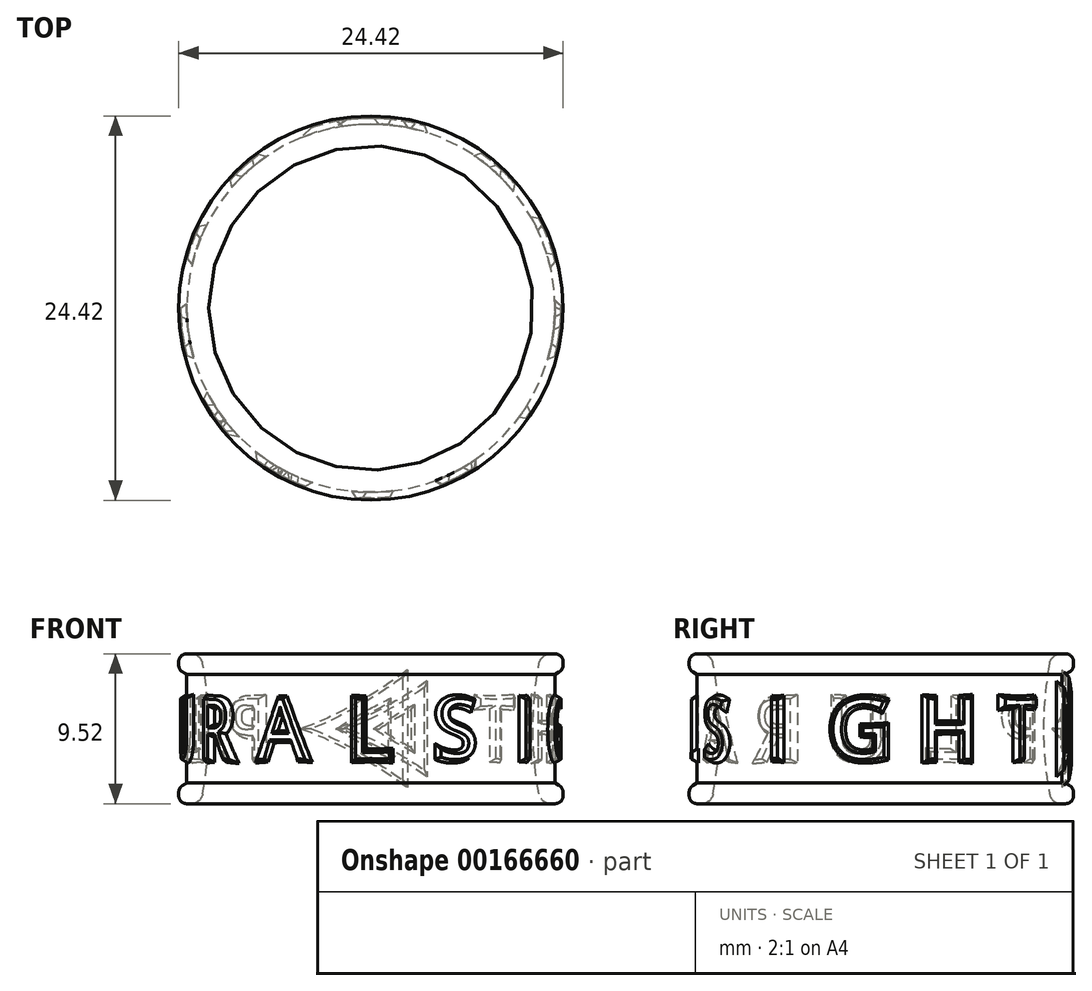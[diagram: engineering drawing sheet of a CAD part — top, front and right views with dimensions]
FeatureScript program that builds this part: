
annotation { "Feature Type Name" : "Feature", "Feature Type Description" : "" }
export const myFeature = defineFeature(function(context is Context, id is Id, definition is map)
    precondition{}
    {
        {
            var Q0;
            Q0=qCreatedBy(makeId("Front.planeOp"),FACE);
            var sketch = newSketch(context, id + "F0", { "sketchPlane" : qUnion([Q0])});
            skLineSegment(sketch, "E0", {"start": v(0, 0) * mm, "end": v(0, 13.93) * mm, "construction": true});
            skLineSegment(sketch, "E1", {"start": v(0, 0) * mm, "end": v(32.88, 0) * mm, "construction": true});
            skLineSegment(sketch, "E2", {"start": v(11.7, 0) * mm, "end": v(11.7, 3.45) * mm});
            skLineSegment(sketch, "E3", {"start": v(11.7, 3.45) * mm, "end": v(12.2, 3.75) * mm});
            skLineSegment(sketch, "E4", {"start": v(12.2, 3.75) * mm, "end": v(12.2, 4.76) * mm});
            skLineSegment(sketch, "E5", {"start": v(12.2, 4.76) * mm, "end": v(10.8, 4.76) * mm});
            skArc(sketch, "E6", {"start": v(10.8, 4.76) * mm, "mid": v(10.43, 2.4) * mm, "end": v(10.3, 0) * mm});
            skLineSegment(sketch, "E7.MirrorCS", {"start": v(11.7, -3.45) * mm, "end": v(12.2, -3.75) * mm});
            skLineSegment(sketch, "E8.MirrorCS", {"start": v(12.2, -4.76) * mm, "end": v(10.8, -4.76) * mm});
            skLineSegment(sketch, "E9.MirrorCS", {"start": v(12.2, -3.75) * mm, "end": v(12.2, -4.76) * mm});
            skArc(sketch, "E10.MirrorCS", {"start": v(10.8, -4.76) * mm, "mid": v(10.43, -2.4) * mm, "end": v(10.3, 0) * mm});
            skLineSegment(sketch, "E11.MirrorCS", {"start": v(11.7, 0) * mm, "end": v(11.7, -3.45) * mm});
            skSolve(sketch);
        }
        {
            var Q0;
            Q0=makeQuery(id+"F0.imprint","IMPRINT",FACE,{"disambiguationData":[TD([[makeQuery(id+"F0.imprint","IMPRINT",EDGE,{"derivedFrom":sQuery(id+"F0.wireOp",EDGE,"E2")}),1.0]])]});
            var Q1;
            Q1=sQuery(id+"F0.wireOp",EDGE,"E0");
            revolve(context, id + "F1", {"entities" : qUnion([Q0]), "axis" : qUnion([Q1]), "revolveType" : RevolveType.FULL});
        }
        {
            var Q0;
            Q0=qCreatedBy(makeId("Top.planeOp"),FACE);
            var sketch = newSketch(context, id + "F2", { "sketchPlane" : qUnion([Q0])});
            skCircle(sketch, "E12.cCircle", {"center": v(0, 0) * mm, "radius": 12.08 * mm});
            skLineSegment(sketch, "E12.0", {"start": v(-11.99, -1.46) * mm, "end": v(-11.3, 4.28) * mm});
            skLineSegment(sketch, "E12.1", {"start": v(-11.3, 4.28) * mm, "end": v(-8, 9.04) * mm});
            skLineSegment(sketch, "E12.2", {"start": v(-8, 9.04) * mm, "end": v(-2.9, 11.73) * mm});
            skLineSegment(sketch, "E12.3", {"start": v(-2.9, 11.73) * mm, "end": v(2.9, 11.73) * mm});
            skLineSegment(sketch, "E12.4", {"start": v(2.9, 11.73) * mm, "end": v(8, 9.04) * mm});
            skLineSegment(sketch, "E12.5", {"start": v(8, 9.04) * mm, "end": v(11.3, 4.28) * mm});
            skLineSegment(sketch, "E12.6", {"start": v(11.3, 4.28) * mm, "end": v(11.99, -1.46) * mm});
            skLineSegment(sketch, "E12.7", {"start": v(11.99, -1.46) * mm, "end": v(9.94, -6.86) * mm});
            skLineSegment(sketch, "E12.8", {"start": v(9.94, -6.86) * mm, "end": v(5.61, -10.7) * mm});
            skLineSegment(sketch, "E12.9", {"start": v(5.61, -10.7) * mm, "end": v(0, -12.08) * mm});
            skLineSegment(sketch, "E12.10", {"start": v(0, -12.08) * mm, "end": v(-5.61, -10.7) * mm});
            skLineSegment(sketch, "E12.11", {"start": v(-5.61, -10.7) * mm, "end": v(-9.94, -6.86) * mm});
            skLineSegment(sketch, "E12.12", {"start": v(-9.94, -6.86) * mm, "end": v(-11.99, -1.46) * mm});
            skCircle(sketch, "E13.0", {"center": v(0, 0) * mm, "radius": 12.33 * mm});
            skLineSegment(sketch, "E14", {"start": v(0, 0) * mm, "end": v(0, 11.73) * mm});
            skLineSegment(sketch, "E15", {"start": v(0, 0) * mm, "end": v(1.68, 11.96) * mm});
            skLineSegment(sketch, "E16", {"start": v(0, 0) * mm, "end": v(-0.63, 12.06) * mm});
            skLineSegment(sketch, "E17", {"start": v(0, 0) * mm, "end": v(8, 9.04) * mm});
            skLineSegment(sketch, "E18", {"start": v(0, 0) * mm, "end": v(11.3, 4.28) * mm});
            skLineSegment(sketch, "E19", {"start": v(0, 0) * mm, "end": v(11.99, -1.46) * mm});
            skLineSegment(sketch, "E20", {"start": v(0, 0) * mm, "end": v(9.94, -6.86) * mm});
            skLineSegment(sketch, "E21", {"start": v(0, 0) * mm, "end": v(5.61, -10.7) * mm});
            skLineSegment(sketch, "E22", {"start": v(0, 0) * mm, "end": v(0, -12.08) * mm});
            skLineSegment(sketch, "E23", {"start": v(0, 0) * mm, "end": v(-5.61, -10.7) * mm});
            skLineSegment(sketch, "E24", {"start": v(0, 0) * mm, "end": v(-9.94, -6.86) * mm});
            skLineSegment(sketch, "E25", {"start": v(0, 0) * mm, "end": v(-11.99, -1.46) * mm});
            skLineSegment(sketch, "E26", {"start": v(0, 0) * mm, "end": v(-11.3, 4.28) * mm});
            skLineSegment(sketch, "E27", {"start": v(0, 0) * mm, "end": v(-8, 9.04) * mm});
            skCircle(sketch, "E28.0", {"center": v(0, 0) * mm, "radius": 18.68 * mm});
            skSolve(sketch);
        }
        {
            var Q0;
            Q0=sQuery(id+"F2.wireOp",VERTEX,"E14.end");
            var Q1;
            Q1=sQuery(id+"F2.wireOp",EDGE,"E14");
            cPlane(context, id + "F3", {"entities" : qUnion([Q0, Q1]), "cplaneType" : CPlaneType.LINE_POINT, "offset" : 25.4 * mm, "width" : 152.4 * mm, "height" : 152.4 * mm});
        }
        {
            var Q0;
            Q0=sQuery(id+"F2.wireOp",VERTEX,"E15.end");
            var Q1;
            Q1=sQuery(id+"F2.wireOp",EDGE,"E15");
            cPlane(context, id + "F4", {"entities" : qUnion([Q0, Q1]), "cplaneType" : CPlaneType.LINE_POINT, "offset" : 25.4 * mm, "width" : 152.4 * mm, "height" : 152.4 * mm});
        }
        {
            var Q0;
            Q0=qCreatedBy(id+"F4.planeOp",FACE);
            var sketch = newSketch(context, id + "F5", { "sketchPlane" : qUnion([Q0])});
            skLineSegment(sketch, "E29", {"start": v(2.64, 0) * mm, "end": v(-1.68, 2.5) * mm});
            skLineSegment(sketch, "E30", {"start": v(-1.68, 2.5) * mm, "end": v(-1.68, 0) * mm});
            skLineSegment(sketch, "E31.0", {"start": v(-1.17, 1.61) * mm, "end": v(-1.17, 0) * mm});
            skLineSegment(sketch, "E31.1", {"start": v(1.63, 0) * mm, "end": v(-1.17, 1.61) * mm});
            skLineSegment(sketch, "E32.MirrorCS", {"start": v(2.64, 0) * mm, "end": v(-1.68, -2.5) * mm});
            skLineSegment(sketch, "E33.MirrorCS", {"start": v(1.63, 0) * mm, "end": v(-1.17, -1.61) * mm});
            skLineSegment(sketch, "E34.MirrorCS", {"start": v(-1.17, -1.61) * mm, "end": v(-1.17, 0) * mm});
            skLineSegment(sketch, "E35.MirrorCS", {"start": v(-1.68, -2.5) * mm, "end": v(-1.68, 0) * mm});
            skSolve(sketch);
        }
        {
            var Q0;
            Q0=makeQuery(id+"F5.imprint","IMPRINT",FACE,{"disambiguationData":[TD([[makeQuery(id+"F5.imprint","IMPRINT",EDGE,{"derivedFrom":sQuery(id+"F5.wireOp",EDGE,"E29")}),1.0]])]});
            extrude(context, id + "F6", {"entities" : qUnion([Q0]), "operationType" : NewBodyOperationType.ADD, "endBound" : BoundingType.UP_TO_NEXT, "oppositeDirection" : true, "depth" : 25.4 * mm, "hasDraft" : true, "draftAngle" : 30 * degree});
        }
        {
            var Q0;
            Q0=sQuery(id+"F2.wireOp",VERTEX,"E16.end");
            var Q1;
            Q1=sQuery(id+"F2.wireOp",EDGE,"E16");
            cPlane(context, id + "F7", {"entities" : qUnion([Q0, Q1]), "cplaneType" : CPlaneType.LINE_POINT, "offset" : 25.4 * mm, "width" : 152.4 * mm, "height" : 152.4 * mm});
        }
        {
            var Q0;
            Q0=qCreatedBy(id+"F7.planeOp",FACE);
            var sketch = newSketch(context, id + "F8", { "sketchPlane" : qUnion([Q0])});
            skLineSegment(sketch, "E36", {"start": v(2.67, 0) * mm, "end": v(-2.5, 2.98) * mm});
            skLineSegment(sketch, "E37", {"start": v(-2.5, 2.98) * mm, "end": v(-2.5, 0) * mm});
            skLineSegment(sketch, "E38.0", {"start": v(-2, 2.1) * mm, "end": v(-2, 0) * mm});
            skLineSegment(sketch, "E38.1", {"start": v(1.65, 0) * mm, "end": v(-2, 2.1) * mm});
            skLineSegment(sketch, "E39.MirrorCS", {"start": v(1.65, 0) * mm, "end": v(-2, -2.1) * mm});
            skLineSegment(sketch, "E40.MirrorCS", {"start": v(-2, -2.1) * mm, "end": v(-2, 0) * mm});
            skLineSegment(sketch, "E41.MirrorCS", {"start": v(-2.5, -2.98) * mm, "end": v(-2.5, 0) * mm});
            skLineSegment(sketch, "E42.MirrorCS", {"start": v(2.67, 0) * mm, "end": v(-2.5, -2.98) * mm});
            skSolve(sketch);
        }
        {
            var Q0;
            Q0=makeQuery(id+"F8.imprint","IMPRINT",FACE,{"disambiguationData":[TD([[makeQuery(id+"F8.imprint","IMPRINT",EDGE,{"derivedFrom":sQuery(id+"F8.wireOp",EDGE,"E36")}),1.0]])]});
            var Q1;
            Q1=makeQuery(id+"F6.boolean.opBoolean","SPLIT",FACE,{"disambiguationData":[TD([makeQuery(id+"F1.opRevolve","SWEPT_FACE",FACE,{"disambiguationData":[OSD([sQuery(id+"F0.wireOp",EDGE,"E3")])]})])],"derivedFrom":makeQuery(id+"F1.opRevolve","SWEPT_FACE",FACE,{"disambiguationData":[OSD([sQuery(id+"F0.wireOp",EDGE,"E2"),sQuery(id+"F0.wireOp",EDGE,"E11.MirrorCS")])]})});
            extrude(context, id + "F9", {"entities" : qUnion([Q0]), "endBound" : BoundingType.UP_TO_SURFACE, "oppositeDirection" : true, "endBoundEntityFace" : qUnion([Q1]), "depth" : 25.4 * mm, "hasDraft" : true, "draftAngle" : 30 * degree});
        }
        {
            var Q0;
            Q0=sQuery(id+"F2.wireOp",VERTEX,"E12.2.start");
            var Q1;
            Q1=sQuery(id+"F2.wireOp",EDGE,"E27");
            cPlane(context, id + "F10", {"entities" : qUnion([Q0, Q1]), "cplaneType" : CPlaneType.LINE_POINT, "offset" : 25.4 * mm, "width" : 152.4 * mm, "height" : 152.4 * mm});
        }
        {
            var Q0;
            Q0=qCreatedBy(id+"F10.planeOp",FACE);
            var sketch = newSketch(context, id + "F11", { "sketchPlane" : qUnion([Q0])});
            skText(sketch, "E43", { "text": "P", "fontName": "OpenSans-Regular.ttf"});
            const initialGuessF11  = {"E43": [-0.00163, -0.0019, 1, 0, 0.00381]};
            skSetInitialGuess(sketch, initialGuessF11);
            skSolve(sketch);
        }
        {
            var Q0;
            Q0 = qSketchRegion(id + "F11", true);
            extrude(context, id + "F12", {"entities" : qUnion([Q0]), "operationType" : NewBodyOperationType.ADD, "endBound" : BoundingType.UP_TO_NEXT, "oppositeDirection" : true, "depth" : 25.4 * mm, "hasDraft" : true, "draftAngle" : 30 * degree});
        }
        {
            var Q0;
            Q0=sQuery(id+"F2.wireOp",VERTEX,"E26.end");
            var Q1;
            Q1=sQuery(id+"F2.wireOp",EDGE,"E26");
            cPlane(context, id + "F13", {"entities" : qUnion([Q0, Q1]), "cplaneType" : CPlaneType.LINE_POINT, "offset" : 25.4 * mm, "width" : 152.4 * mm, "height" : 152.4 * mm});
        }
        {
            var Q0;
            Q0=qCreatedBy(id+"F13.planeOp",FACE);
            var sketch = newSketch(context, id + "F14", { "sketchPlane" : qUnion([Q0])});
            skText(sketch, "E44", { "text": "L", "fontName": "OpenSans-Regular.ttf"});
            const initialGuessF14  = {"E44": [-0.00148, -0.0019, 1, 0, 0.00381]};
            skSetInitialGuess(sketch, initialGuessF14);
            skSolve(sketch);
        }
        {
            var Q0;
            Q0=makeQuery(id+"F14.imprint","IMPRINT",FACE,{"disambiguationData":[TD([[makeQuery(id+"F14.imprint","IMPRINT",EDGE,{"derivedFrom":sQuery(id+"F14.wireOp",EDGE,"E44.sketch_text.stroke-0")}),-1.0]])]});
            extrude(context, id + "F15", {"entities" : qUnion([Q0]), "operationType" : NewBodyOperationType.ADD, "endBound" : BoundingType.UP_TO_NEXT, "oppositeDirection" : true, "depth" : 25.4 * mm, "hasDraft" : true, "draftAngle" : 30 * degree});
        }
        {
            var Q0;
            Q0=sQuery(id+"F2.wireOp",VERTEX,"E12.12.end");
            var Q1;
            Q1=sQuery(id+"F2.wireOp",EDGE,"E25");
            cPlane(context, id + "F16", {"entities" : qUnion([Q0, Q1]), "cplaneType" : CPlaneType.LINE_POINT, "offset" : 25.4 * mm, "width" : 152.4 * mm, "height" : 152.4 * mm});
        }
        {
            var Q0;
            Q0=qCreatedBy(id+"F16.planeOp",FACE);
            var sketch = newSketch(context, id + "F17", { "sketchPlane" : qUnion([Q0])});
            skText(sketch, "E45", { "text": "U", "fontName": "OpenSans-Regular.ttf"});
            const initialGuessF17  = {"E45": [-0.00186, -0.0019, 1, 0, 0.00381]};
            skSetInitialGuess(sketch, initialGuessF17);
            skSolve(sketch);
        }
        {
            var Q0;
            Q0=makeQuery(id+"F17.imprint","IMPRINT",FACE,{"disambiguationData":[TD([[makeQuery(id+"F17.imprint","IMPRINT",EDGE,{"derivedFrom":sQuery(id+"F17.wireOp",EDGE,"E45.sketch_text.stroke-0")}),-1.0]])]});
            extrude(context, id + "F18", {"entities" : qUnion([Q0]), "operationType" : NewBodyOperationType.ADD, "endBound" : BoundingType.UP_TO_NEXT, "oppositeDirection" : true, "depth" : 25.4 * mm, "hasDraft" : true, "draftAngle" : 30 * degree});
        }
        {
            var Q0;
            Q0=sQuery(id+"F2.wireOp",VERTEX,"E12.12.start");
            var Q1;
            Q1=sQuery(id+"F2.wireOp",EDGE,"E24");
            cPlane(context, id + "F19", {"entities" : qUnion([Q0, Q1]), "cplaneType" : CPlaneType.LINE_POINT, "offset" : 25.4 * mm, "width" : 152.4 * mm, "height" : 152.4 * mm});
        }
        {
            var Q0;
            Q0=qCreatedBy(id+"F19.planeOp",FACE);
            var sketch = newSketch(context, id + "F20", { "sketchPlane" : qUnion([Q0])});
            skText(sketch, "E46", { "text": "R", "fontName": "OpenSans-Regular.ttf"});
            const initialGuessF20  = {"E46": [-0.00176, -0.0019, 1, 0, 0.0038]};
            skSetInitialGuess(sketch, initialGuessF20);
            skSolve(sketch);
        }
        {
            var Q0;
            Q0 = qSketchRegion(id + "F20", true);
            extrude(context, id + "F21", {"entities" : qUnion([Q0]), "operationType" : NewBodyOperationType.ADD, "endBound" : BoundingType.UP_TO_NEXT, "oppositeDirection" : true, "depth" : 25.4 * mm, "hasDraft" : true, "draftAngle" : 30 * degree});
        }
        {
            var Q0;
            Q0=sQuery(id+"F2.wireOp",VERTEX,"E23.end");
            var Q1;
            Q1=sQuery(id+"F2.wireOp",EDGE,"E23");
            cPlane(context, id + "F22", {"entities" : qUnion([Q0, Q1]), "cplaneType" : CPlaneType.LINE_POINT, "offset" : 25.4 * mm, "width" : 152.4 * mm, "height" : 152.4 * mm});
        }
        {
            var Q0;
            Q0=qCreatedBy(id+"F22.planeOp",FACE);
            var sketch = newSketch(context, id + "F23", { "sketchPlane" : qUnion([Q0])});
            skText(sketch, "E47", { "text": "A", "fontName": "OpenSans-Regular.ttf"});
            const initialGuessF23  = {"E47": [-0.00185, -0.0019, 1, 0, 0.00381]};
            skSetInitialGuess(sketch, initialGuessF23);
            skSolve(sketch);
        }
        {
            var Q0;
            Q0=makeQuery(id+"F23.imprint","IMPRINT",FACE,{"disambiguationData":[TD([[makeQuery(id+"F23.imprint","IMPRINT",EDGE,{"derivedFrom":sQuery(id+"F23.wireOp",EDGE,"E47.sketch_text.stroke-0")}),-1.0]])]});
            extrude(context, id + "F24", {"entities" : qUnion([Q0]), "operationType" : NewBodyOperationType.ADD, "endBound" : BoundingType.UP_TO_NEXT, "oppositeDirection" : true, "depth" : 25.4 * mm, "hasDraft" : true, "draftAngle" : 25 * degree});
        }
        {
            var Q0;
            Q0=sQuery(id+"F2.wireOp",VERTEX,"E12.10.start");
            var Q1;
            Q1=sQuery(id+"F2.wireOp",EDGE,"E22");
            cPlane(context, id + "F25", {"entities" : qUnion([Q0, Q1]), "cplaneType" : CPlaneType.LINE_POINT, "offset" : 25.4 * mm, "width" : 152.4 * mm, "height" : 152.4 * mm});
        }
        {
            var Q0;
            Q0=qCreatedBy(id+"F25.planeOp",FACE);
            var sketch = newSketch(context, id + "F26", { "sketchPlane" : qUnion([Q0])});
            skText(sketch, "E48", { "text": "L", "fontName": "OpenSans-Regular.ttf"});
            const initialGuessF26  = {"E48": [-0.00148, -0.0019, 1, 0, 0.0038]};
            skSetInitialGuess(sketch, initialGuessF26);
            skSolve(sketch);
        }
        {
            var Q0;
            Q0=makeQuery(id+"F26.imprint","IMPRINT",FACE,{"disambiguationData":[TD([[makeQuery(id+"F26.imprint","IMPRINT",EDGE,{"derivedFrom":sQuery(id+"F26.wireOp",EDGE,"E48.sketch_text.stroke-0")}),-1.0]])]});
            extrude(context, id + "F27", {"entities" : qUnion([Q0]), "operationType" : NewBodyOperationType.ADD, "endBound" : BoundingType.UP_TO_NEXT, "oppositeDirection" : true, "depth" : 25.4 * mm, "hasDraft" : true, "draftAngle" : 30 * degree});
        }
        {
            var Q0;
            Q0=sQuery(id+"F2.wireOp",VERTEX,"E21.end");
            var Q1;
            Q1=sQuery(id+"F2.wireOp",EDGE,"E21");
            cPlane(context, id + "F28", {"entities" : qUnion([Q0, Q1]), "cplaneType" : CPlaneType.LINE_POINT, "offset" : 25.4 * mm, "width" : 152.4 * mm, "height" : 152.4 * mm});
        }
        {
            var Q0;
            Q0=qCreatedBy(id+"F28.planeOp",FACE);
            var sketch = newSketch(context, id + "F29", { "sketchPlane" : qUnion([Q0])});
            skText(sketch, "E49", { "text": "S", "fontName": "OpenSans-Regular.ttf"});
            const initialGuessF29  = {"E49": [-0.0015, -0.0019, 1, 0, 0.00381]};
            skSetInitialGuess(sketch, initialGuessF29);
            skSolve(sketch);
        }
        {
            var Q0;
            Q0=makeQuery(id+"F29.imprint","IMPRINT",FACE,{"disambiguationData":[TD([[makeQuery(id+"F29.imprint","IMPRINT",EDGE,{"derivedFrom":sQuery(id+"F29.wireOp",EDGE,"E49.sketch_text.stroke-0")}),-1.0]])]});
            extrude(context, id + "F30", {"entities" : qUnion([Q0]), "operationType" : NewBodyOperationType.ADD, "endBound" : BoundingType.UP_TO_NEXT, "oppositeDirection" : true, "depth" : 25.4 * mm, "hasDraft" : true, "draftAngle" : 30 * degree});
        }
        {
            var Q0;
            Q0=sQuery(id+"F2.wireOp",VERTEX,"E12.7.end");
            var Q1;
            Q1=sQuery(id+"F2.wireOp",EDGE,"E20");
            cPlane(context, id + "F31", {"entities" : qUnion([Q0, Q1]), "cplaneType" : CPlaneType.LINE_POINT, "offset" : 25.4 * mm, "width" : 152.4 * mm, "height" : 152.4 * mm});
        }
        {
            var Q0;
            Q0=qCreatedBy(id+"F31.planeOp",FACE);
            var sketch = newSketch(context, id + "F32", { "sketchPlane" : qUnion([Q0])});
            skText(sketch, "E50", { "text": "I", "fontName": "OpenSans-Regular.ttf"});
            const initialGuessF32  = {"E50": [-0.00065, -0.0019, 1, 0, 0.00381]};
            skSetInitialGuess(sketch, initialGuessF32);
            skSolve(sketch);
        }
        {
            var Q0;
            Q0=makeQuery(id+"F32.imprint","IMPRINT",FACE,{"disambiguationData":[TD([[makeQuery(id+"F32.imprint","IMPRINT",EDGE,{"derivedFrom":sQuery(id+"F32.wireOp",EDGE,"E50.sketch_text.stroke-0")}),-1.0]])]});
            extrude(context, id + "F33", {"entities" : qUnion([Q0]), "operationType" : NewBodyOperationType.ADD, "endBound" : BoundingType.UP_TO_NEXT, "oppositeDirection" : true, "depth" : 25.4 * mm, "hasDraft" : true, "draftAngle" : 30 * degree});
        }
        {
            var Q0;
            Q0=sQuery(id+"F2.wireOp",VERTEX,"E12.7.start");
            var Q1;
            Q1=sQuery(id+"F2.wireOp",EDGE,"E19");
            cPlane(context, id + "F34", {"entities" : qUnion([Q0, Q1]), "cplaneType" : CPlaneType.LINE_POINT, "offset" : 25.4 * mm, "width" : 152.4 * mm, "height" : 152.4 * mm});
        }
        {
            var Q0;
            Q0=qCreatedBy(id+"F34.planeOp",FACE);
            var sketch = newSketch(context, id + "F35", { "sketchPlane" : qUnion([Q0])});
            skText(sketch, "E51", { "text": "G", "fontName": "OpenSans-Regular.ttf"});
            const initialGuessF35  = {"E51": [-0.0019, -0.0019, 1, 0, 0.00381]};
            skSetInitialGuess(sketch, initialGuessF35);
            skSolve(sketch);
        }
        {
            var Q0;
            Q0=makeQuery(id+"F35.imprint","IMPRINT",FACE,{"disambiguationData":[TD([[makeQuery(id+"F35.imprint","IMPRINT",EDGE,{"derivedFrom":sQuery(id+"F35.wireOp",EDGE,"E51.sketch_text.stroke-0")}),-1.0]])]});
            extrude(context, id + "F36", {"entities" : qUnion([Q0]), "operationType" : NewBodyOperationType.ADD, "endBound" : BoundingType.UP_TO_NEXT, "oppositeDirection" : true, "depth" : 25.4 * mm, "hasDraft" : true, "draftAngle" : 30 * degree});
        }
        {
            var Q0;
            Q0=sQuery(id+"F2.wireOp",VERTEX,"E18.end");
            var Q1;
            Q1=sQuery(id+"F2.wireOp",EDGE,"E18");
            cPlane(context, id + "F37", {"entities" : qUnion([Q0, Q1]), "cplaneType" : CPlaneType.LINE_POINT, "offset" : 25.4 * mm, "width" : 152.4 * mm, "height" : 152.4 * mm});
        }
        {
            var Q0;
            Q0=qCreatedBy(id+"F37.planeOp",FACE);
            var sketch = newSketch(context, id + "F38", { "sketchPlane" : qUnion([Q0])});
            skText(sketch, "E52", { "text": "H", "fontName": "OpenSans-Regular.ttf"});
            const initialGuessF38  = {"E52": [-0.00187, -0.0019, 1, 0, 0.00381]};
            skSetInitialGuess(sketch, initialGuessF38);
            skSolve(sketch);
        }
        {
            var Q0;
            Q0=makeQuery(id+"F38.imprint","IMPRINT",FACE,{"disambiguationData":[TD([[makeQuery(id+"F38.imprint","IMPRINT",EDGE,{"derivedFrom":sQuery(id+"F38.wireOp",EDGE,"E52.sketch_text.stroke-0")}),-1.0]])]});
            extrude(context, id + "F39", {"entities" : qUnion([Q0]), "operationType" : NewBodyOperationType.ADD, "endBound" : BoundingType.UP_TO_NEXT, "oppositeDirection" : true, "depth" : 25.4 * mm, "hasDraft" : true, "draftAngle" : 30 * degree});
        }
        {
            var Q0;
            Q0=sQuery(id+"F2.wireOp",VERTEX,"E12.5.start");
            var Q1;
            Q1=sQuery(id+"F2.wireOp",EDGE,"E17");
            cPlane(context, id + "F40", {"entities" : qUnion([Q0, Q1]), "cplaneType" : CPlaneType.LINE_POINT, "offset" : 25.4 * mm, "width" : 152.4 * mm, "height" : 152.4 * mm});
        }
        {
            var Q0;
            Q0=qCreatedBy(id+"F40.planeOp",FACE);
            var sketch = newSketch(context, id + "F41", { "sketchPlane" : qUnion([Q0])});
            skText(sketch, "E53", { "text": "T", "fontName": "OpenSans-Regular.ttf"});
            const initialGuessF41  = {"E53": [-0.00161, -0.0019, 1, 0, 0.0038]};
            skSetInitialGuess(sketch, initialGuessF41);
            skSolve(sketch);
        }
        {
            var Q0;
            Q0=makeQuery(id+"F41.imprint","IMPRINT",FACE,{"disambiguationData":[TD([[makeQuery(id+"F41.imprint","IMPRINT",EDGE,{"derivedFrom":sQuery(id+"F41.wireOp",EDGE,"E53.sketch_text.stroke-0")}),-1.0]])]});
            extrude(context, id + "F42", {"entities" : qUnion([Q0]), "operationType" : NewBodyOperationType.ADD, "endBound" : BoundingType.UP_TO_NEXT, "oppositeDirection" : true, "depth" : 25.4 * mm, "hasDraft" : true, "draftAngle" : 30 * degree});
        }
        {
            var Q0;
            Q0=makeQuery(id+"F2.imprint","IMPRINT",FACE,{"disambiguationData":[TD([[makeQuery(id+"F2.imprint","IMPRINT",EDGE,{"derivedFrom":sQuery(id+"F2.wireOp",EDGE,"E13.0")}),-1.0]])]});
            extrude(context, id + "F43", {"entities" : qUnion([Q0]), "operationType" : NewBodyOperationType.REMOVE, "endBound" : BoundingType.THROUGH_ALL, "oppositeDirection" : true, "depth" : 25.4 * mm, "hasSecondDirection" : true, "secondDirectionBound" : SecondDirectionBoundingType.THROUGH_ALL, "secondDirectionOppositeDirection" : false, "secondDirectionDepth" : 25.4 * mm});
        }
        {
            var Q0;
            Q0=makeQuery(id+"F2.imprint","IMPRINT",FACE,{"disambiguationData":[TD([[makeQuery(id+"F2.imprint","IMPRINT",EDGE,{"derivedFrom":sQuery(id+"F2.wireOp",EDGE,"E13.0")}),1.0]])]});
            var Q1;
            Q1=makeQuery(id+"F2.imprint","IMPRINT",FACE,{"disambiguationData":[TD([[makeQuery(id+"F2.imprint","IMPRINT",EDGE,{"derivedFrom":sQuery(id+"F2.wireOp",EDGE,"E13.0")}),-1.0]])]});
            extrude(context, id + "F44", {"entities" : qUnion([Q0, Q1]), "operationType" : NewBodyOperationType.REMOVE, "oppositeDirection" : true, "depth" : 3.56 * mm, "hasSecondDirection" : true, "secondDirectionOppositeDirection" : false, "secondDirectionDepth" : 3.56 * mm});
        }
        {
            var Q0;
            Q0=makeQuery(id+"F1.opRevolve","SWEPT_FACE",FACE,{"disambiguationData":[OSD([sQuery(id+"F0.wireOp",EDGE,"E6"),sQuery(id+"F0.wireOp",EDGE,"E10.MirrorCS")])]});
            fillet(context, id + "F45", {"entities" : qUnion([Q0]), "radius" : 0.76 * mm, "tangentPropagation" : true, "allowEdgeOverflow" : false});
        }
        {
            var Q0;
            Q0=makeQuery(id+"F1.opRevolve","SWEPT_FACE",FACE,{"disambiguationData":[OSD([sQuery(id+"F0.wireOp",EDGE,"E4")])]});
            var Q1;
            Q1=makeQuery(id+"F1.opRevolve","SWEPT_FACE",FACE,{"disambiguationData":[OSD([sQuery(id+"F0.wireOp",EDGE,"E9.MirrorCS")])]});
            fillet(context, id + "F46", {"entities" : qUnion([Q0, Q1]), "radius" : 0.5 * mm, "tangentPropagation" : true, "allowEdgeOverflow" : false});
        }
    });
